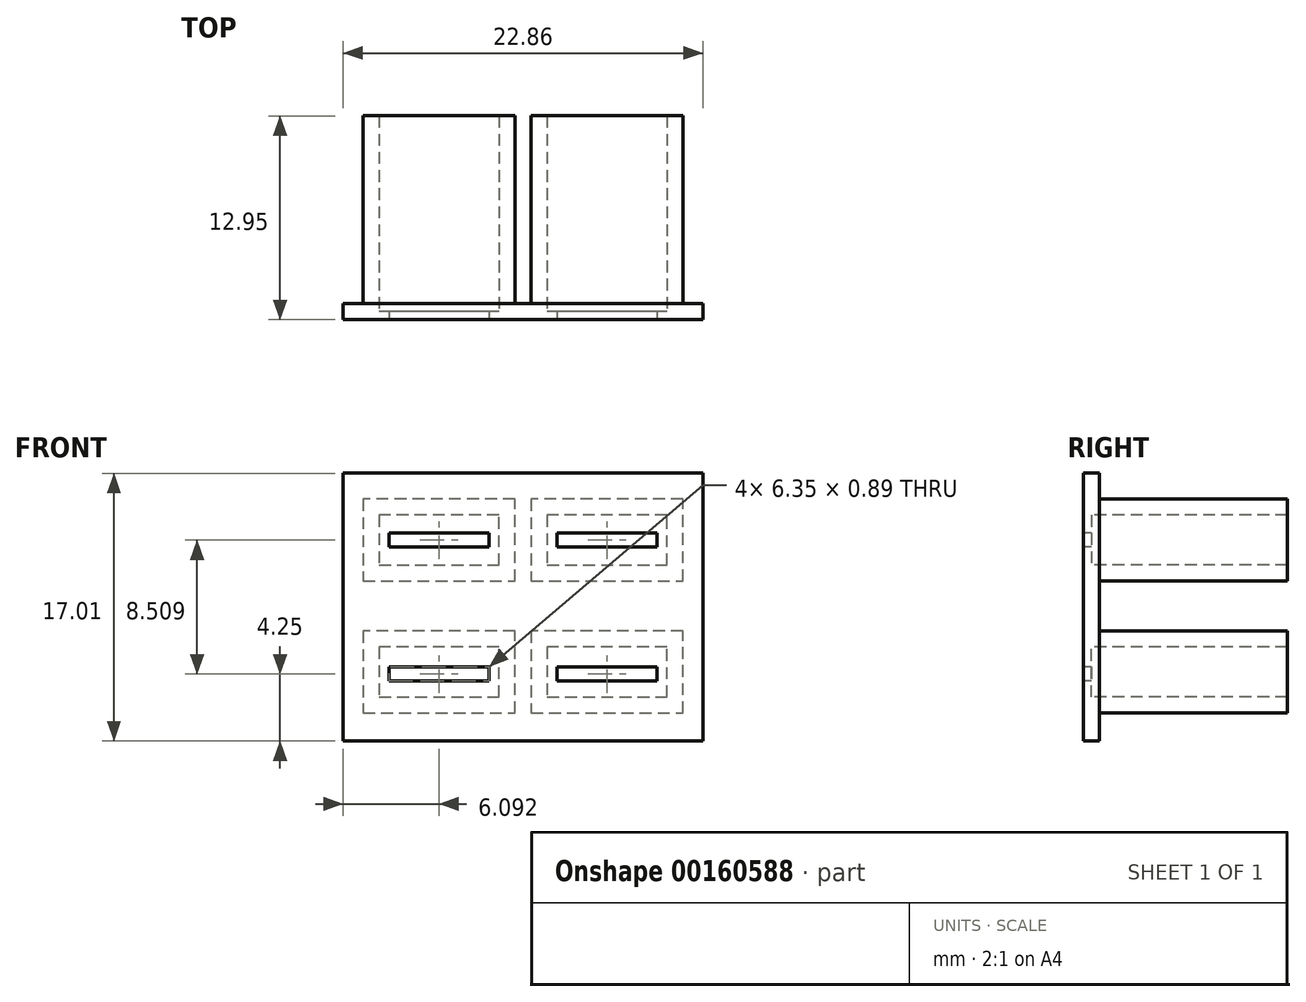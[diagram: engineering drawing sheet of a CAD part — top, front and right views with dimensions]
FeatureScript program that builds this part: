
annotation { "Feature Type Name" : "Feature", "Feature Type Description" : "" }
export const myFeature = defineFeature(function(context is Context, id is Id, definition is map)
    precondition{}
    {
        {
            var Q0;
            Q0=qCreatedBy(makeId("Front.planeOp"),FACE);
            var sketch = newSketch(context, id + "F0", { "sketchPlane" : qUnion([Q0])});
            skLineSegment(sketch, "E0", {"start": v(-22.83, 35) * mm, "end": v(-22.83, 12.13) * mm});
            skLineSegment(sketch, "E1", {"start": v(-22.83, 12.13) * mm, "end": v(2.57, 12.13) * mm});
            skLineSegment(sketch, "E2", {"start": v(2.57, 12.13) * mm, "end": v(2.57, 35) * mm});
            skLineSegment(sketch, "E3", {"start": v(2.57, 35) * mm, "end": v(-22.83, 35) * mm});
            skSolve(sketch);
        }
        {
            var Q0;
            Q0=qSketchRegion(id+"F0",true);
            extrude(context, id + "F1", {"entities" : qUnion([Q0]), "oppositeDirection" : true, "depth" : 1.02 * mm});
        }
        {
            var Q0;
            Q0=makeQuery(id+"F1.opExtrude","CAP_FACE",FACE,{"disambiguationData":[OSD([sQuery(id+"F0.wireOp",EDGE,"E0"),sQuery(id+"F0.wireOp",EDGE,"E1"),sQuery(id+"F0.wireOp",EDGE,"E2"),sQuery(id+"F0.wireOp",EDGE,"E3")])],"isStart":true});
            var sketch = newSketch(context, id + "F2", { "sketchPlane" : qUnion([Q0])});
            skLineSegment(sketch, "E4", {"start": v(-17.37, 28.13) * mm, "end": v(-17.37, 27.24) * mm});
            skLineSegment(sketch, "E5", {"start": v(-17.37, 27.24) * mm, "end": v(-11.02, 27.24) * mm});
            skLineSegment(sketch, "E6", {"start": v(-11.02, 27.24) * mm, "end": v(-11.02, 28.13) * mm});
            skLineSegment(sketch, "E7", {"start": v(-11.02, 28.13) * mm, "end": v(-17.37, 28.13) * mm});
            skLineSegment(sketch, "E8", {"start": v(-6.7, 28.13) * mm, "end": v(-6.7, 27.24) * mm});
            skLineSegment(sketch, "E9", {"start": v(-6.7, 27.24) * mm, "end": v(-0.36, 27.24) * mm});
            skLineSegment(sketch, "E10", {"start": v(-0.36, 27.24) * mm, "end": v(-0.36, 28.13) * mm});
            skLineSegment(sketch, "E11", {"start": v(-0.36, 28.13) * mm, "end": v(-6.7, 28.13) * mm});
            skLineSegment(sketch, "E12", {"start": v(-17.37, 19.62) * mm, "end": v(-17.37, 18.74) * mm});
            skLineSegment(sketch, "E13", {"start": v(-17.37, 18.74) * mm, "end": v(-11.02, 18.74) * mm});
            skLineSegment(sketch, "E14", {"start": v(-11.02, 18.74) * mm, "end": v(-11.02, 19.62) * mm});
            skLineSegment(sketch, "E15", {"start": v(-11.02, 19.62) * mm, "end": v(-17.37, 19.62) * mm});
            skLineSegment(sketch, "E16", {"start": v(-6.7, 19.62) * mm, "end": v(-6.7, 18.74) * mm});
            skLineSegment(sketch, "E17", {"start": v(-6.7, 18.74) * mm, "end": v(-0.36, 18.74) * mm});
            skLineSegment(sketch, "E18", {"start": v(-0.36, 18.74) * mm, "end": v(-0.36, 19.62) * mm});
            skLineSegment(sketch, "E19", {"start": v(-0.36, 19.62) * mm, "end": v(-6.7, 19.62) * mm});
            skSolve(sketch);
        }
        {
            var Q0;
            Q0=qSketchRegion(id+"F2",true);
            extrude(context, id + "F3", {"entities" : qUnion([Q0]), "operationType" : NewBodyOperationType.REMOVE, "oppositeDirection" : true, "depth" : 25.4 * mm});
        }
        {
            var Q0;
            Q0=makeQuery(id+"F1.opExtrude","CAP_FACE",FACE,{"disambiguationData":[OSD([sQuery(id+"F0.wireOp",EDGE,"E0"),sQuery(id+"F0.wireOp",EDGE,"E1"),sQuery(id+"F0.wireOp",EDGE,"E2"),sQuery(id+"F0.wireOp",EDGE,"E3")])],"isStart":true});
            var sketch = newSketch(context, id + "F4", { "sketchPlane" : qUnion([Q0])});
            skLineSegment(sketch, "E20", {"start": v(-18, 29.28) * mm, "end": v(-18, 26.1) * mm});
            skLineSegment(sketch, "E21", {"start": v(-18, 26.1) * mm, "end": v(-10.39, 26.1) * mm});
            skLineSegment(sketch, "E22", {"start": v(-10.39, 26.1) * mm, "end": v(-10.39, 29.28) * mm});
            skLineSegment(sketch, "E23", {"start": v(-10.39, 29.28) * mm, "end": v(-18, 29.28) * mm});
            skLineSegment(sketch, "E24", {"start": v(-7.34, 29.28) * mm, "end": v(-7.34, 26.1) * mm});
            skLineSegment(sketch, "E25", {"start": v(-7.34, 26.1) * mm, "end": v(0.28, 26.1) * mm});
            skLineSegment(sketch, "E26", {"start": v(0.28, 26.1) * mm, "end": v(0.28, 29.28) * mm});
            skLineSegment(sketch, "E27", {"start": v(0.28, 29.28) * mm, "end": v(-7.34, 29.28) * mm});
            skLineSegment(sketch, "E28", {"start": v(-19.02, 30.3) * mm, "end": v(-19.02, 25.09) * mm});
            skLineSegment(sketch, "E29", {"start": v(-19.02, 25.09) * mm, "end": v(-9.37, 25.09) * mm});
            skLineSegment(sketch, "E30", {"start": v(-9.37, 25.09) * mm, "end": v(-9.37, 30.3) * mm});
            skLineSegment(sketch, "E31", {"start": v(-9.37, 30.3) * mm, "end": v(-19.02, 30.3) * mm});
            skLineSegment(sketch, "E32", {"start": v(-8.36, 30.3) * mm, "end": v(-8.36, 25.09) * mm});
            skLineSegment(sketch, "E33", {"start": v(-8.36, 25.09) * mm, "end": v(1.3, 25.09) * mm});
            skLineSegment(sketch, "E34", {"start": v(1.3, 25.09) * mm, "end": v(1.3, 30.3) * mm});
            skLineSegment(sketch, "E35", {"start": v(1.3, 30.3) * mm, "end": v(-8.36, 30.3) * mm});
            skLineSegment(sketch, "E36.0.1.0", {"start": v(-9.37, 21.91) * mm, "end": v(-19.02, 21.91) * mm});
            skLineSegment(sketch, "E36.0.1.1", {"start": v(-10.39, 20.9) * mm, "end": v(-18, 20.9) * mm});
            skLineSegment(sketch, "E36.0.1.2", {"start": v(-10.39, 17.72) * mm, "end": v(-10.39, 20.9) * mm});
            skLineSegment(sketch, "E36.0.1.3", {"start": v(-18, 17.72) * mm, "end": v(-10.39, 17.72) * mm});
            skLineSegment(sketch, "E36.0.1.4", {"start": v(-18, 20.9) * mm, "end": v(-18, 17.72) * mm});
            skLineSegment(sketch, "E36.0.1.5", {"start": v(-9.37, 16.7) * mm, "end": v(-9.37, 21.91) * mm});
            skLineSegment(sketch, "E36.0.1.6", {"start": v(-19.02, 16.7) * mm, "end": v(-9.37, 16.7) * mm});
            skLineSegment(sketch, "E36.0.1.7", {"start": v(-19.02, 21.91) * mm, "end": v(-19.02, 16.7) * mm});
            skLineSegment(sketch, "E36.0.1.8", {"start": v(-7.34, 17.72) * mm, "end": v(0.28, 17.72) * mm});
            skLineSegment(sketch, "E36.0.1.9", {"start": v(0.28, 20.9) * mm, "end": v(-7.34, 20.9) * mm});
            skLineSegment(sketch, "E36.0.1.10", {"start": v(-7.34, 20.9) * mm, "end": v(-7.34, 17.72) * mm});
            skLineSegment(sketch, "E36.0.1.11", {"start": v(0.28, 17.72) * mm, "end": v(0.28, 20.9) * mm});
            skLineSegment(sketch, "E36.0.1.12", {"start": v(1.3, 16.7) * mm, "end": v(1.3, 21.91) * mm});
            skLineSegment(sketch, "E36.0.1.13", {"start": v(1.3, 21.91) * mm, "end": v(-8.36, 21.91) * mm});
            skLineSegment(sketch, "E36.0.1.14", {"start": v(-8.36, 21.91) * mm, "end": v(-8.36, 16.7) * mm});
            skLineSegment(sketch, "E36.0.1.15", {"start": v(-8.36, 16.7) * mm, "end": v(1.3, 16.7) * mm});
            skLineSegment(sketch, "E36.direction1", {"start": v(-19.02, 30.3) * mm, "end": v(6.38, 30.3) * mm, "construction": true});
            skLineSegment(sketch, "E36.direction2", {"start": v(-19.02, 30.3) * mm, "end": v(-19.02, 21.91) * mm, "construction": true});
            skSolve(sketch);
        }
        {
            var Q0;
            Q0=qSketchRegion(id+"F4",true);
            extrude(context, id + "F5", {"entities" : qUnion([Q0]), "operationType" : NewBodyOperationType.ADD, "oppositeDirection" : true, "depth" : 12.95 * mm});
        }
        {
            var Q0;
            Q0=makeQuery(id+"F1.opExtrude","CAP_FACE",FACE,{"disambiguationData":[OSD([sQuery(id+"F0.wireOp",EDGE,"E0"),sQuery(id+"F0.wireOp",EDGE,"E1"),sQuery(id+"F0.wireOp",EDGE,"E2"),sQuery(id+"F0.wireOp",EDGE,"E3")])],"isStart":true});
            var sketch = newSketch(context, id + "F6", { "sketchPlane" : qUnion([Q0])});
            skLineSegment(sketch, "E37", {"start": v(-22.83, 14.93) * mm, "end": v(2.57, 14.93) * mm});
            skLineSegment(sketch, "E38", {"start": v(2.57, 14.93) * mm, "end": v(2.57, 12.13) * mm});
            skLineSegment(sketch, "E39", {"start": v(2.57, 12.13) * mm, "end": v(-22.83, 12.13) * mm});
            skLineSegment(sketch, "E40", {"start": v(-22.83, 12.13) * mm, "end": v(-22.83, 14.93) * mm});
            skLineSegment(sketch, "E41", {"start": v(-22.83, 35) * mm, "end": v(-22.83, 31.94) * mm});
            skLineSegment(sketch, "E42", {"start": v(-22.83, 31.94) * mm, "end": v(2.57, 31.94) * mm});
            skLineSegment(sketch, "E43", {"start": v(2.57, 31.94) * mm, "end": v(2.57, 35) * mm});
            skLineSegment(sketch, "E44", {"start": v(2.57, 35) * mm, "end": v(-22.83, 35) * mm});
            skSolve(sketch);
        }
        {
            var Q0;
            Q0=qSketchRegion(id+"F6",true);
            extrude(context, id + "F7", {"entities" : qUnion([Q0]), "operationType" : NewBodyOperationType.REMOVE, "endBound" : BoundingType.THROUGH_ALL, "oppositeDirection" : true, "depth" : 25.4 * mm});
        }
        {
            var Q0;
            Q0=makeQuery(id+"F1.opExtrude","CAP_FACE",FACE,{"disambiguationData":[OSD([sQuery(id+"F0.wireOp",EDGE,"E0"),sQuery(id+"F0.wireOp",EDGE,"E1"),sQuery(id+"F0.wireOp",EDGE,"E2"),sQuery(id+"F0.wireOp",EDGE,"E3")])],"isStart":true});
            var sketch = newSketch(context, id + "F8", { "sketchPlane" : qUnion([Q0])});
            skLineSegment(sketch, "E45", {"start": v(-22.83, 31.94) * mm, "end": v(-22.83, 14.93) * mm});
            skLineSegment(sketch, "E46", {"start": v(-22.83, 31.94) * mm, "end": v(-20.3, 31.94) * mm});
            skLineSegment(sketch, "E47", {"start": v(-20.3, 31.94) * mm, "end": v(-20.3, 14.93) * mm});
            skLineSegment(sketch, "E48", {"start": v(-20.3, 14.93) * mm, "end": v(-22.83, 14.93) * mm});
            skSolve(sketch);
        }
        {
            var Q0;
            Q0=qSketchRegion(id+"F8",true);
            extrude(context, id + "F9", {"entities" : qUnion([Q0]), "operationType" : NewBodyOperationType.REMOVE, "oppositeDirection" : true, "depth" : 25.4 * mm});
        }
        {
            var Q0;
            Q0=makeQuery(id+"F5.boolean.opBoolean","SPLIT",FACE,{"disambiguationData":[TD([makeQuery(id+"F3.boolean.opBoolean","COPY",FACE,{"derivedFrom":makeQuery(id+"F3.opExtrude","SWEPT_FACE",FACE,{"disambiguationData":[OSD([sQuery(id+"F2.wireOp",EDGE,"E4")])]})})])],"derivedFrom":makeQuery(id+"F1.opExtrude","CAP_FACE",FACE,{"disambiguationData":[OSD([sQuery(id+"F0.wireOp",EDGE,"E0"),sQuery(id+"F0.wireOp",EDGE,"E1"),sQuery(id+"F0.wireOp",EDGE,"E2"),sQuery(id+"F0.wireOp",EDGE,"E3")])],"isStart":false})});
            var Q1;
            Q1=makeQuery(id+"F5.boolean.opBoolean","SPLIT",FACE,{"disambiguationData":[TD([makeQuery(id+"F3.boolean.opBoolean","COPY",FACE,{"derivedFrom":makeQuery(id+"F3.opExtrude","SWEPT_FACE",FACE,{"disambiguationData":[OSD([sQuery(id+"F2.wireOp",EDGE,"E16")])]})})])],"derivedFrom":makeQuery(id+"F1.opExtrude","CAP_FACE",FACE,{"disambiguationData":[OSD([sQuery(id+"F0.wireOp",EDGE,"E0"),sQuery(id+"F0.wireOp",EDGE,"E1"),sQuery(id+"F0.wireOp",EDGE,"E2"),sQuery(id+"F0.wireOp",EDGE,"E3")])],"isStart":false})});
            var Q2;
            Q2=makeQuery(id+"F5.boolean.opBoolean","SPLIT",FACE,{"disambiguationData":[TD([makeQuery(id+"F3.boolean.opBoolean","COPY",FACE,{"derivedFrom":makeQuery(id+"F3.opExtrude","SWEPT_FACE",FACE,{"disambiguationData":[OSD([sQuery(id+"F2.wireOp",EDGE,"E12")])]})})])],"derivedFrom":makeQuery(id+"F1.opExtrude","CAP_FACE",FACE,{"disambiguationData":[OSD([sQuery(id+"F0.wireOp",EDGE,"E0"),sQuery(id+"F0.wireOp",EDGE,"E1"),sQuery(id+"F0.wireOp",EDGE,"E2"),sQuery(id+"F0.wireOp",EDGE,"E3")])],"isStart":false})});
            var Q3;
            Q3=makeQuery(id+"F5.boolean.opBoolean","SPLIT",FACE,{"disambiguationData":[TD([makeQuery(id+"F3.boolean.opBoolean","COPY",FACE,{"derivedFrom":makeQuery(id+"F3.opExtrude","SWEPT_FACE",FACE,{"disambiguationData":[OSD([sQuery(id+"F2.wireOp",EDGE,"E8")])]})})])],"derivedFrom":makeQuery(id+"F1.opExtrude","CAP_FACE",FACE,{"disambiguationData":[OSD([sQuery(id+"F0.wireOp",EDGE,"E0"),sQuery(id+"F0.wireOp",EDGE,"E1"),sQuery(id+"F0.wireOp",EDGE,"E2"),sQuery(id+"F0.wireOp",EDGE,"E3")])],"isStart":false})});
            extrude(context, id + "F10", {"entities" : qUnion([Q0, Q1, Q2, Q3]), "operationType" : NewBodyOperationType.REMOVE, "oppositeDirection" : true, "depth" : 0.5 * mm});
        }
    });
